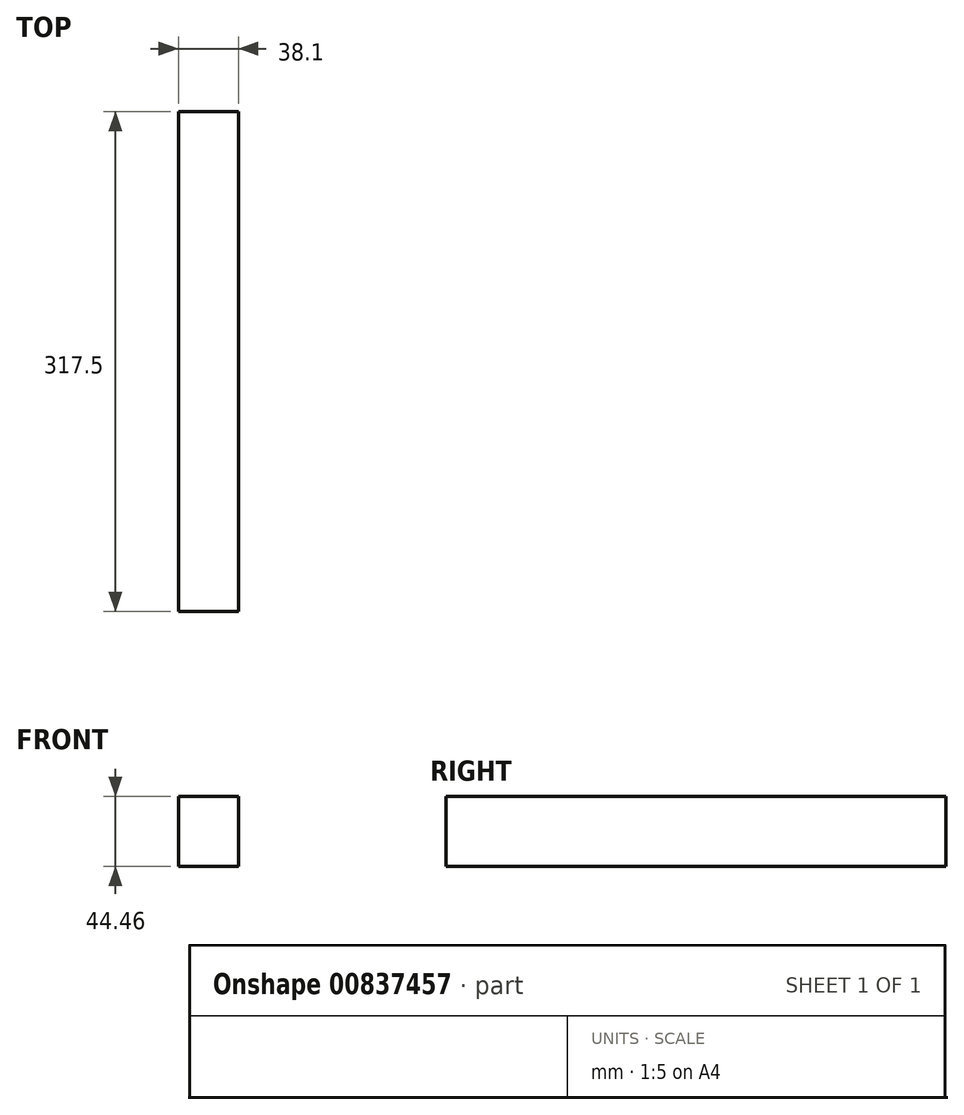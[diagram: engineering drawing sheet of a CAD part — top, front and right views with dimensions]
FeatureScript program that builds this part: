
annotation { "Feature Type Name" : "Feature", "Feature Type Description" : "" }
export const myFeature = defineFeature(function(context is Context, id is Id, definition is map)
    precondition{}
    {
        {
            var Q0;
            Q0=qCreatedBy(makeId("Front.planeOp"),FACE);
            var sketch = newSketch(context, id + "F0", { "sketchPlane" : qUnion([Q0])});
            skLineSegment(sketch, "E0.bottom", {"start": v(19.05, 22.23) * mm, "end": v(-19.05, 22.23) * mm});
            skLineSegment(sketch, "E0.top", {"start": v(19.05, -22.23) * mm, "end": v(-19.05, -22.23) * mm});
            skLineSegment(sketch, "E0.left", {"start": v(19.05, 22.23) * mm, "end": v(19.05, -22.23) * mm});
            skLineSegment(sketch, "E0.right", {"start": v(-19.05, 22.23) * mm, "end": v(-19.05, -22.23) * mm});
            skPoint(sketch, "E0.middle", {"position": v(0, 0) * mm});
            skSolve(sketch);
        }
        {
            var Q0;
            Q0=makeQuery(id+"F0.imprint","IMPRINT",FACE,{"disambiguationData":[TD([[makeQuery(id+"F0.imprint","IMPRINT",EDGE,{"derivedFrom":sQuery(id+"F0.wireOp",EDGE,"E0.bottom")}),1.0]])]});
            extrude(context, id + "F1", {"entities" : qUnion([Q0]), "endBound" : BoundingType.SYMMETRIC, "depth" : 317.5 * mm, "offsetDistance" : 25.4 * mm});
        }
    });
